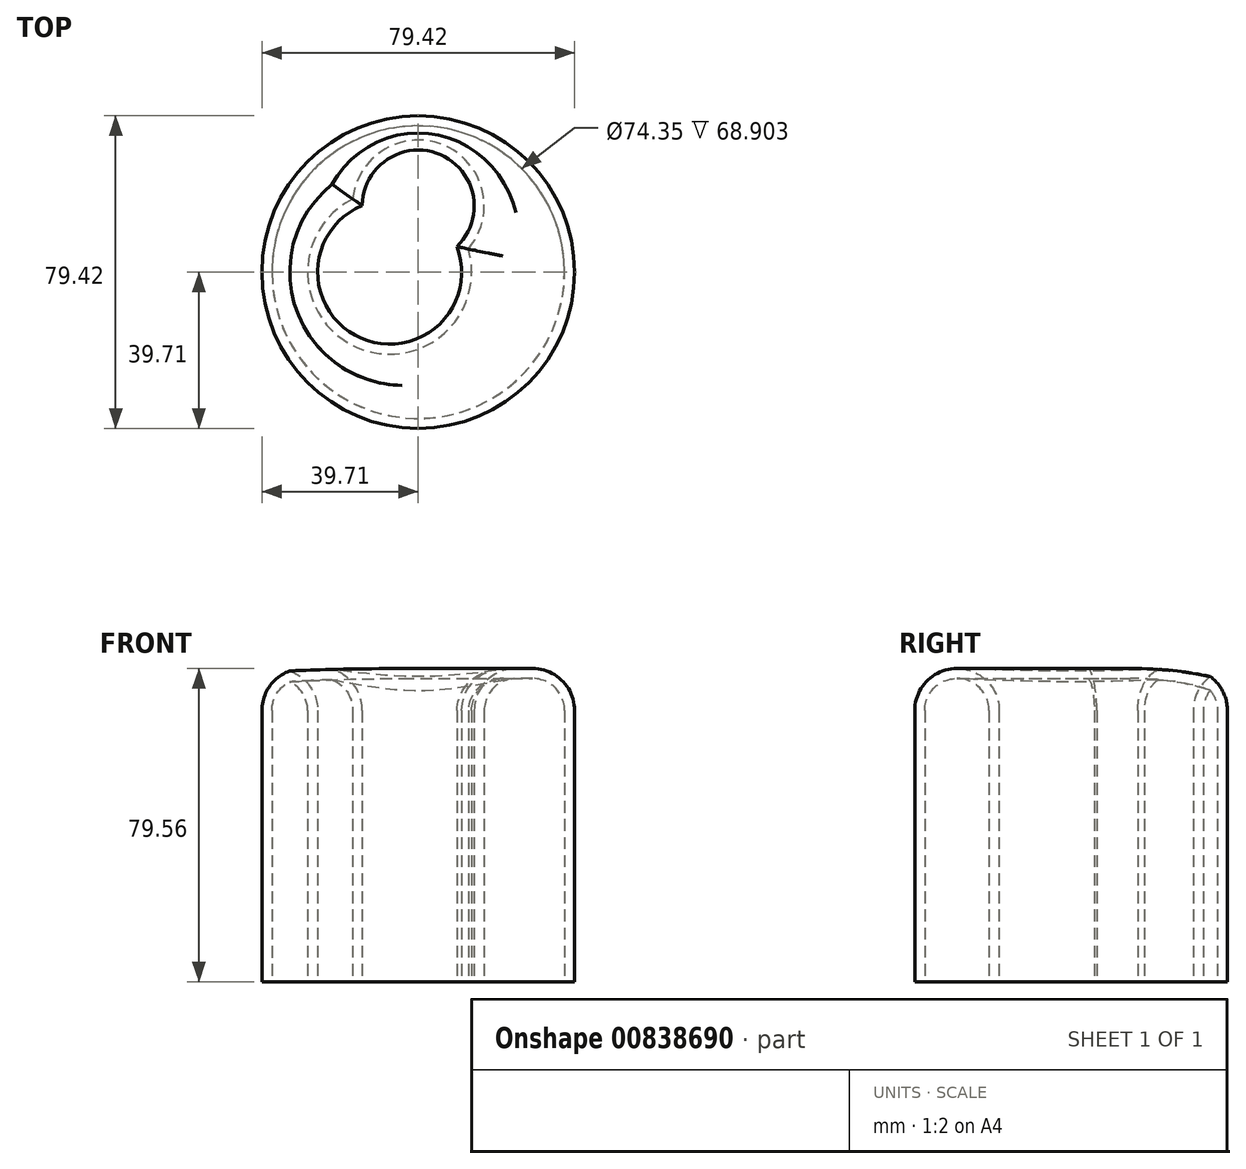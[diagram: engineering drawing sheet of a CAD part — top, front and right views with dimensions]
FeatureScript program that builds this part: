
annotation { "Feature Type Name" : "Feature", "Feature Type Description" : "" }
export const myFeature = defineFeature(function(context is Context, id is Id, definition is map)
    precondition{}
    {
        {
            var Q0;
            Q0=qCreatedBy(makeId("Top.planeOp"),FACE);
            var sketch = newSketch(context, id + "F0", { "sketchPlane" : qUnion([Q0])});
            skCircle(sketch, "E0", {"center": v(0, 0) * mm, "radius": 39.71 * mm});
            skCircle(sketch, "E1", {"center": v(0, 16.8) * mm, "radius": 14.22 * mm});
            skCircle(sketch, "E2", {"center": v(-7.26, 0) * mm, "radius": 18.3 * mm});
            skSolve(sketch);
        }
        {
            var Q0;
            Q0=makeQuery(id+"F0.imprint","IMPRINT",FACE,{"disambiguationData":[TD([[makeQuery(id+"F0.imprint","IMPRINT",EDGE,{"derivedFrom":sQuery(id+"F0.wireOp",EDGE,"E0")}),1.0]])]});
            extrude(context, id + "F1", {"entities" : qUnion([Q0]), "endBound" : BoundingType.SYMMETRIC, "depth" : 79.56 * mm, "offsetDistance" : 25.4 * mm});
        }
        {
            var Q0;
            Q0=makeQuery(id+"F1.opExtrude","CAP_FACE",FACE,{"disambiguationData":[OSD([sQuery(id+"F0.wireOp",EDGE,"E0"),sQuery(id+"F0.wireOp",EDGE,"E1"),sQuery(id+"F0.wireOp",EDGE,"E2")])],"isStart":false});
            fillet(context, id + "F2", {"entities" : qUnion([Q0]), "radius" : 10.65 * mm, "tangentPropagation" : true, "allowEdgeOverflow" : false});
        }
        {
            var Q0;
            Q0=makeQuery(id+"F1.opExtrude","CAP_FACE",FACE,{"disambiguationData":[OSD([sQuery(id+"F0.wireOp",EDGE,"E0"),sQuery(id+"F0.wireOp",EDGE,"E1"),sQuery(id+"F0.wireOp",EDGE,"E2")])],"isStart":true});
            shell(context, id + "F3", {"entities" : qUnion([Q0]), "thickness" : 2.54 * mm});
        }
    });
